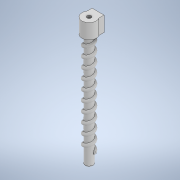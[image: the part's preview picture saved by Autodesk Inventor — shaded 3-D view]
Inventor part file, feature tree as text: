
AUTODESK INVENTOR PART (.ipt)
format: ipt  version: 2020 (Build 240168000, 168)  size: 302,080 bytes
history: native  units: in
note: dims shown in document units (in); Inventor stores cm internally (conversion verified against a paired STEP export)
features: sketch x5, extrude x4, fillet x3, helix x1
ambient origin geometry x8: Origin, YZ Plane, XZ Plane, XY Plane, X Axis, Y Axis, Z Axis, Center Point
bodies: Solid1 (feature_tree)
feature tree (13):
  extrude  "Extrusion1"  Depth=3.3465in TaperAngle=0.0deg
  helix  "Coil1"  [1 undecoded]
  fillet  "Fillet1"  Radius=0.0312in
  fillet  "Fillet2"  Radius=0.0312in
  fillet  "Fillet3"  Radius=0.0018in
  extrude  "Extrusion3"  Depth=0.375in
  extrude  "Extrusion4"  Depth=0.3937in
  extrude  "Extrusion5"  Depth=0.3937in
  sketch  "Sketch1"  dims[d0=0.2067in d1=3.3465in d2=0.0in d3=0.0469in]
  sketch  "Sketch2"  dims[d4=0.25in d5=1.0in d6=4.7244in d7=0.0in d8=90.0deg d9=90.0deg d10=0.0in d11=0.0in d14=0.0312in d15=0.0312in d16=0.0312in d17=0.0018in]
  sketch  "Sketch4"  dims[d18=0.25in d19=0.375in]
  sketch  "Sketch5"  dims[d20=0.3937in d21=0.0in d22=0.315in]
  sketch  "Sketch6"  dims[d23=0.2362in d24=0.0984in d25=0.2362in d26=0.0in d27=0.1083in d28=0.3937in d29=0.0in]
note: 1 required parameter value undecoded (feature->parameter linkage not recoverable at this tier; creation-order binding heuristic only, values carry confidence <= 0.55)
